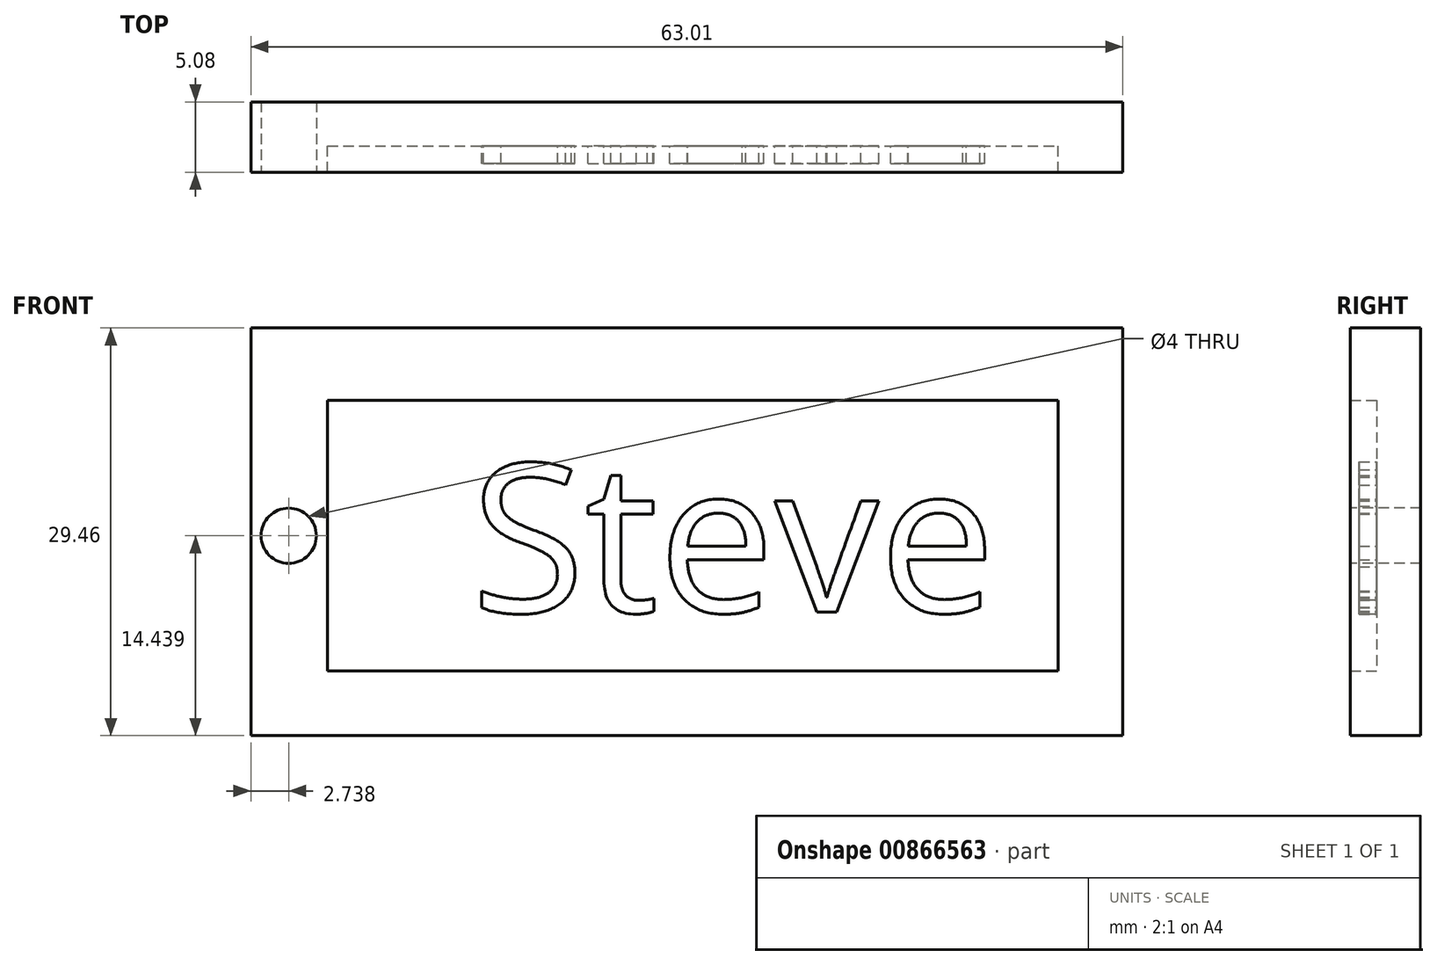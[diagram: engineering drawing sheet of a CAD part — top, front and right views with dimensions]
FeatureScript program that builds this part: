
annotation { "Feature Type Name" : "Feature", "Feature Type Description" : "" }
export const myFeature = defineFeature(function(context is Context, id is Id, definition is map)
    precondition{}
    {
        {
            var Q0;
            Q0=qCreatedBy(makeId("Front.planeOp"),FACE);
            var sketch = newSketch(context, id + "F0", { "sketchPlane" : qUnion([Q0])});
            skLineSegment(sketch, "E0.bottom", {"start": v(0, 34.06) * mm, "end": v(63, 34.06) * mm});
            skLineSegment(sketch, "E0.top", {"start": v(0, 4.6) * mm, "end": v(63, 4.6) * mm});
            skLineSegment(sketch, "E0.left", {"start": v(0, 34.06) * mm, "end": v(0, 4.6) * mm});
            skLineSegment(sketch, "E0.right", {"start": v(63, 34.06) * mm, "end": v(63, 4.6) * mm});
            skLineSegment(sketch, "E1.bottom", {"start": v(5.54, 28.81) * mm, "end": v(58.34, 28.81) * mm});
            skLineSegment(sketch, "E1.top", {"start": v(5.54, 9.27) * mm, "end": v(58.34, 9.27) * mm});
            skLineSegment(sketch, "E1.left", {"start": v(5.54, 28.81) * mm, "end": v(5.54, 9.27) * mm});
            skLineSegment(sketch, "E1.right", {"start": v(58.34, 28.81) * mm, "end": v(58.34, 9.27) * mm});
            skSolve(sketch);
        }
        {
            var Q0;
            Q0 = qSketchRegion(id + "F0", true);
            extrude(context, id + "F1", {"entities" : qUnion([Q0]), "depth" : 5.08 * mm, "offsetDistance" : 25.4 * mm});
        }
        {
            var Q0;
            Q0=makeQuery(id+"F0.imprint","IMPRINT",FACE,{"disambiguationData":[TD([[makeQuery(id+"F0.imprint","IMPRINT",EDGE,{"derivedFrom":sQuery(id+"F0.wireOp",EDGE,"E1.bottom")}),-1.0]])]});
            extrude(context, id + "F2", {"entities" : qUnion([Q0]), "operationType" : NewBodyOperationType.ADD, "depth" : 3.17 * mm, "offsetDistance" : 25.4 * mm});
        }
        {
            var Q0;
            Q0=makeQuery(id+"F1.opExtrude","CAP_FACE",FACE,{"disambiguationData":[OSD([sQuery(id+"F0.wireOp",EDGE,"E0.bottom"),sQuery(id+"F0.wireOp",EDGE,"E0.top"),sQuery(id+"F0.wireOp",EDGE,"E0.left"),sQuery(id+"F0.wireOp",EDGE,"E0.right"),sQuery(id+"F0.wireOp",EDGE,"E1.bottom"),sQuery(id+"F0.wireOp",EDGE,"E1.top"),sQuery(id+"F0.wireOp",EDGE,"E1.left"),sQuery(id+"F0.wireOp",EDGE,"E1.right")])],"isStart":false});
            var sketch = newSketch(context, id + "F3", { "sketchPlane" : qUnion([Q0])});
            skCircle(sketch, "E2", {"center": v(2.74, 19.04) * mm, "radius": 2 * mm});
            skPoint(sketch, "E3", {"position": v(5.54, 19.04) * mm});
            skSolve(sketch);
        }
        {
            var Q0;
            Q0=makeQuery(id+"F2.opExtrude","CAP_FACE",FACE,{"disambiguationData":[OSD([sQuery(id+"F0.wireOp",EDGE,"E1.bottom"),sQuery(id+"F0.wireOp",EDGE,"E1.top"),sQuery(id+"F0.wireOp",EDGE,"E1.left"),sQuery(id+"F0.wireOp",EDGE,"E1.right")])],"isStart":false});
            var sketch = newSketch(context, id + "F4", { "sketchPlane" : qUnion([Q0])});
            skText(sketch, "E4", { "text": "Steve", "fontName": "OpenSans-Regular.ttf"});
            const initialGuessF4  = {"E4": [0.0159, 0.01351, 1, 0, 0.01081]};
            skSetInitialGuess(sketch, initialGuessF4);
            skSolve(sketch);
        }
        {
            var Q0;
            Q0 = qSketchRegion(id + "F4", true);
            extrude(context, id + "F5", {"entities" : qUnion([Q0]), "operationType" : NewBodyOperationType.ADD, "depth" : 1.27 * mm, "offsetDistance" : 25.4 * mm});
        }
        {
            var Q0;
            Q0 = qSketchRegion(id + "F3", true);
            extrude(context, id + "F6", {"entities" : qUnion([Q0]), "operationType" : NewBodyOperationType.REMOVE, "oppositeDirection" : true, "depth" : 25.4 * mm, "offsetDistance" : 25.4 * mm});
        }
    });
